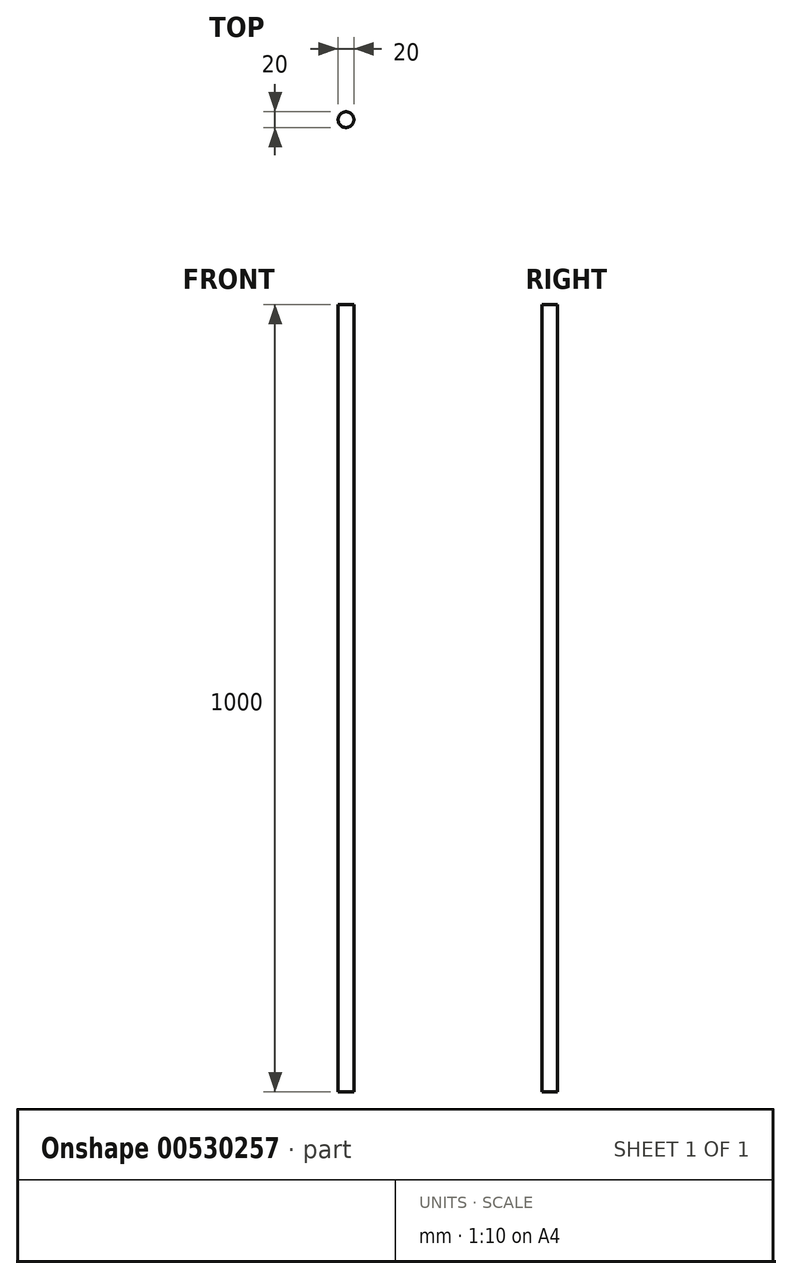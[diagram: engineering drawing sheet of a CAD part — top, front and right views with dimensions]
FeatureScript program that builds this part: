
annotation { "Feature Type Name" : "Feature", "Feature Type Description" : "" }
export const myFeature = defineFeature(function(context is Context, id is Id, definition is map)
    precondition{}
    {
        {
            var Q0;
            Q0=qCreatedBy(makeId("Top.planeOp"),FACE);
            var sketch = newSketch(context, id + "F0", { "sketchPlane" : qUnion([Q0])});
            skCircle(sketch, "E0", {"center": v(0, 0) * mm, "radius": 10 * mm});
            skSolve(sketch);
        }
        {
            var Q0;
            Q0=makeQuery(id+"F0.imprint","IMPRINT",FACE,{"disambiguationData":[TD([[makeQuery(id+"F0.imprint","IMPRINT",EDGE,{"derivedFrom":sQuery(id+"F0.wireOp",EDGE,"E0")}),1.0]])]});
            extrude(context, id + "F1", {"entities" : qUnion([Q0]), "depth" : 1000 * mm, "offsetDistance" : 25 * mm});
        }
    });
